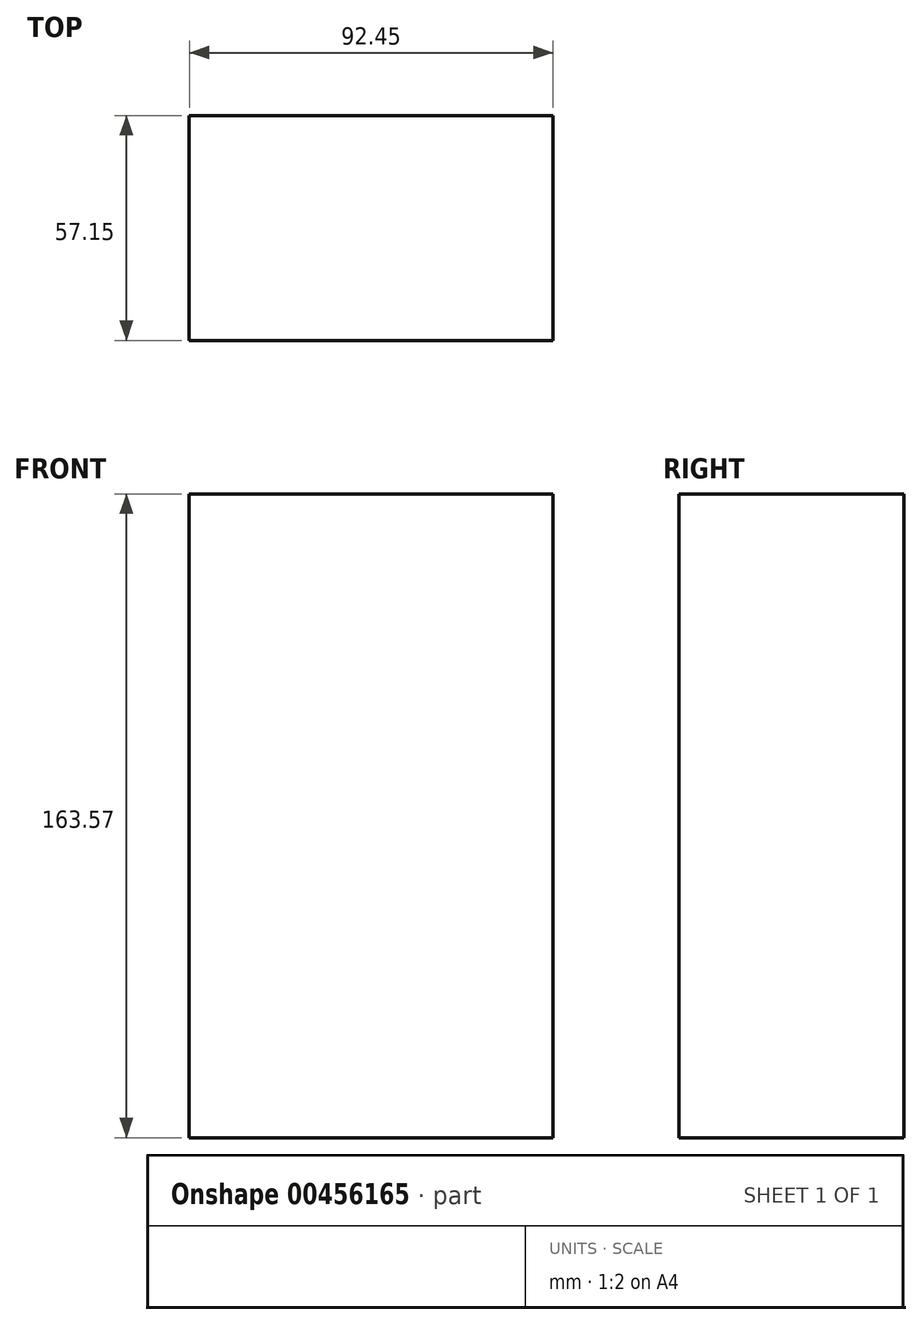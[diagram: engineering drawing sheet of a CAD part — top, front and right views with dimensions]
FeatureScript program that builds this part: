
annotation { "Feature Type Name" : "Feature", "Feature Type Description" : "" }
export const myFeature = defineFeature(function(context is Context, id is Id, definition is map)
    precondition{}
    {
        {
            var Q0;
            Q0=qCreatedBy(makeId("Front.planeOp"),FACE);
            var sketch = newSketch(context, id + "F0", { "sketchPlane" : qUnion([Q0])});
            skLineSegment(sketch, "E0", {"start": v(-53.62, 107.28) * mm, "end": v(-53.62, -56.3) * mm});
            skLineSegment(sketch, "E1", {"start": v(-53.62, -56.3) * mm, "end": v(38.83, -56.3) * mm});
            skLineSegment(sketch, "E2", {"start": v(38.83, -56.3) * mm, "end": v(38.83, 107.28) * mm});
            skLineSegment(sketch, "E3", {"start": v(38.83, 107.28) * mm, "end": v(-53.62, 107.28) * mm});
            skSolve(sketch);
        }
        {
            var Q0;
            Q0 = qSketchRegion(id + "F0", true);
            extrude(context, id + "F1", {"entities" : qUnion([Q0]), "depth" : 57.15 * mm});
        }
    });
